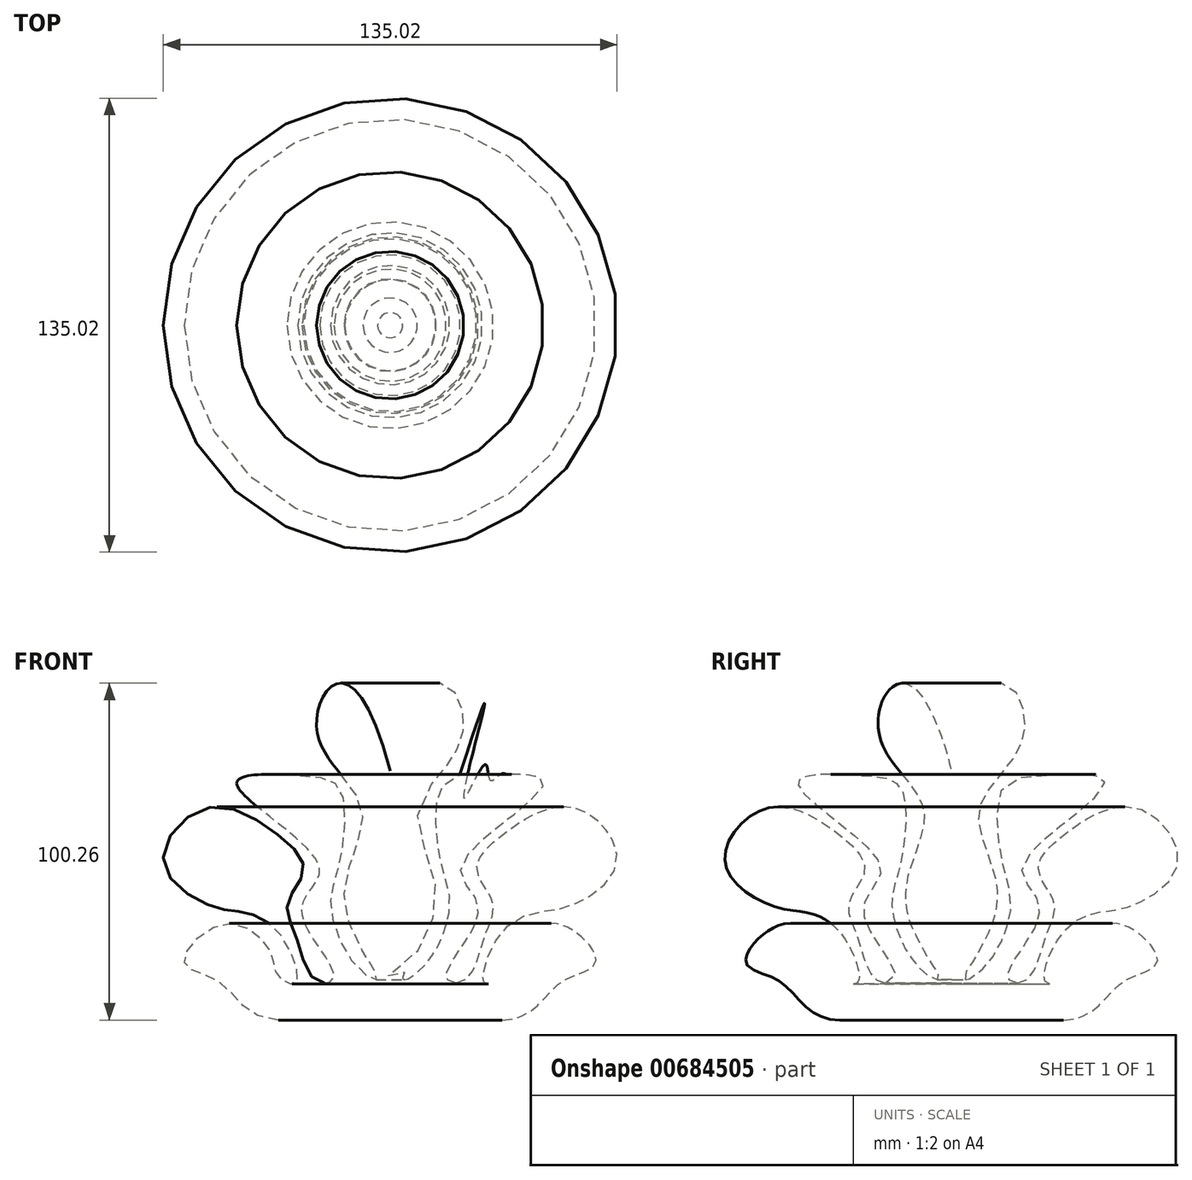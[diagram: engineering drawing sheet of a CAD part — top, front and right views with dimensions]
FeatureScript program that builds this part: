
annotation { "Feature Type Name" : "Feature", "Feature Type Description" : "" }
export const myFeature = defineFeature(function(context is Context, id is Id, definition is map)
    precondition{}
    {
        {
            var Q0;
            Q0=qCreatedBy(makeId("Front.planeOp"),FACE);
            var sketch = newSketch(context, id + "F0", { "sketchPlane" : qUnion([Q0])});
            skLineSegment(sketch, "E0", {"start": v(0, 0) * mm, "end": v(-33.3, 0) * mm});
            skFitSpline(sketch, "E1", {"points": [v(-33.3, 0) * mm, v(-51.04, 11.43) * mm, v(-61.24, 17.28) * mm, v(-49.1, 28.73) * mm, v(-35.6, 20.03) * mm, v(-33.3, 12.93) * mm, v(-28.04, 11.1) * mm, v(-33.3, 26.21) * mm, v(-44.3, 32.16) * mm, v(-53.45, 34) * mm, v(-67.42, 46.82) * mm, v(-54.83, 63.07) * mm, v(-33.3, 55.06) * mm, v(-25.75, 44.53) * mm, v(-30.56, 34.91) * mm, v(-28.04, 24.84) * mm, v(-22.1, 11.79) * mm, v(-16.83, 12.48) * mm, v(-24.15, 26.21) * mm, v(-25.3, 36.51) * mm, v(-21.4, 46.59) * mm, v(-45.67, 70.4) * mm, v(-25.98, 72.68) * mm, v(-14.77, 68.33) * mm, v(-15.45, 45.44) * mm, v(-17.74, 34.22) * mm, v(-10.19, 16.14) * mm, v(-3.78, 12.25) * mm, v(-13.62, 34.45) * mm, v(-8.36, 62.84) * mm, v(-21.93, 88.63) * mm, v(0, 74.06) * mm], "startDerivative": vector(-787.57, 7.22) * mm, "endDerivative": vector(730.57, -2844.07) * mm});
            skLineSegment(sketch, "E2", {"start": v(0, 74.06) * mm, "end": v(0, 0) * mm});
            skSolve(sketch);
        }
        {
            var Q0;
            Q0=sQuery(id+"F0.wireOp",EDGE,"E0");
            var Q1;
            Q1=sQuery(id+"F0.wireOp",EDGE,"E1");
            var Q2;
            Q2=sQuery(id+"F0.wireOp",EDGE,"E2");
            revolve(context, id + "F1", {"bodyType" : ToolBodyType.SURFACE, "surfaceEntities" : qUnion([Q0, Q1]), "axis" : qUnion([Q2]), "revolveType" : RevolveType.FULL});
        }
    });
